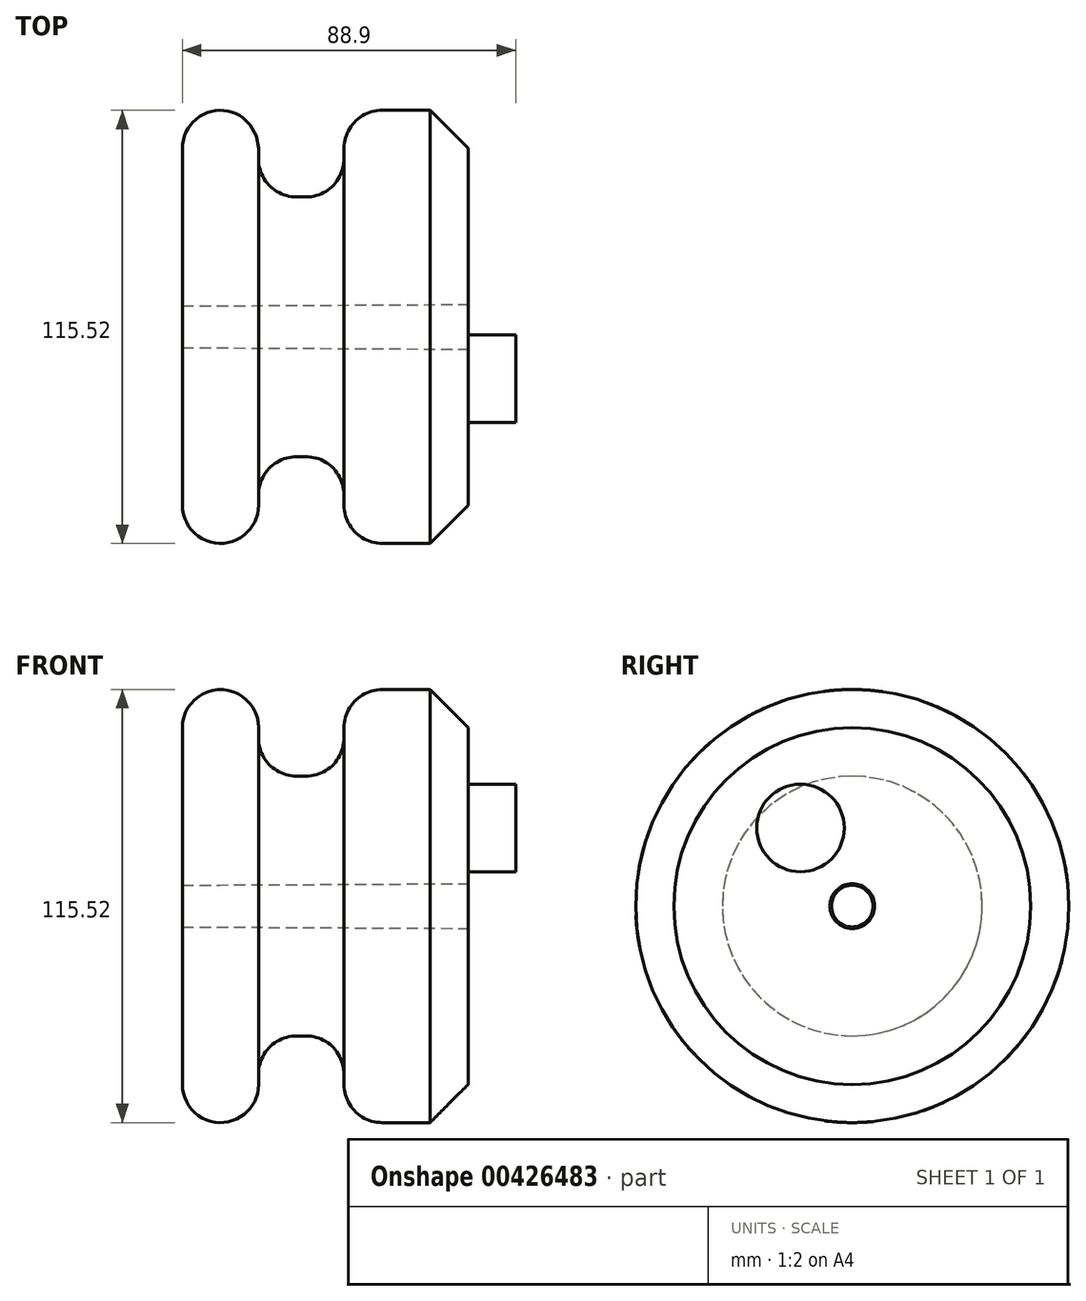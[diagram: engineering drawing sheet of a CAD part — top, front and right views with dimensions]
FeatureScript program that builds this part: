
annotation { "Feature Type Name" : "Feature", "Feature Type Description" : "" }
export const myFeature = defineFeature(function(context is Context, id is Id, definition is map)
    precondition{}
    {
        {
            var Q0;
            Q0=qCreatedBy(makeId("Top.planeOp"),FACE);
            var sketch = newSketch(context, id + "F0", { "sketchPlane" : qUnion([Q0])});
            skLineSegment(sketch, "E0", {"start": v(-62.92, -5.56) * mm, "end": v(-62.92, -57.76) * mm});
            skLineSegment(sketch, "E1", {"start": v(-42.6, -57.76) * mm, "end": v(-42.6, -34.64) * mm});
            skLineSegment(sketch, "E2", {"start": v(-42.6, -34.64) * mm, "end": v(-19.82, -34.64) * mm});
            skLineSegment(sketch, "E3", {"start": v(-19.82, -34.64) * mm, "end": v(-19.82, -57.76) * mm});
            skLineSegment(sketch, "E4", {"start": v(-19.82, -57.76) * mm, "end": v(13.28, -57.76) * mm});
            skLineSegment(sketch, "E5", {"start": v(13.28, -57.76) * mm, "end": v(13.28, -5.97) * mm});
            skLineSegment(sketch, "E6", {"start": v(13.28, -5.97) * mm, "end": v(-62.92, -5.56) * mm});
            skLineSegment(sketch, "E7", {"start": v(-42.6, -57.76) * mm, "end": v(-62.92, -57.76) * mm});
            skLineSegment(sketch, "E8", {"start": v(-61.6, 0) * mm, "end": v(66.9, 0) * mm, "construction": true});
            skSolve(sketch);
        }
        {
            var Q0;
            Q0=makeQuery(id+"F0.imprint","IMPRINT",FACE,{"disambiguationData":[TD([[makeQuery(id+"F0.imprint","IMPRINT",EDGE,{"derivedFrom":sQuery(id+"F0.wireOp",EDGE,"E0")}),1.0]])]});
            var Q1;
            Q1=sQuery(id+"F0.wireOp",EDGE,"E8");
            revolve(context, id + "F1", {"entities" : qUnion([Q0]), "axis" : qUnion([Q1]), "revolveType" : RevolveType.FULL});
        }
        {
            var Q0;
            Q0=makeQuery(id+"F1.opRevolve","SWEPT_EDGE",EDGE,{"disambiguationData":[OSD([sQuery(id+"F0.wireOp",EDGE,"E0"),sQuery(id+"F0.wireOp",EDGE,"E7")])]});
            fillet(context, id + "F2", {"entities" : qUnion([Q0]), "radius" : 10.16 * mm, "tangentPropagation" : true, "allowEdgeOverflow" : false});
        }
        {
            var Q0;
            Q0=makeQuery(id+"F1.opRevolve","SWEPT_EDGE",EDGE,{"disambiguationData":[OSD([sQuery(id+"F0.wireOp",EDGE,"E3"),sQuery(id+"F0.wireOp",EDGE,"E4")])]});
            var Q1;
            {var subQ0=sQuery(id+"F0.wireOp",EDGE,"E4");Q1=makeQuery(id+"F39CXcwR2j7VM4l_1.opFillet","BLEND_EDGE",EDGE,{"blendedFrom":[makeQuery(id+"F1.opRevolve","SWEPT_EDGE",EDGE,{"disambiguationData":[OSD([subQ0,sQuery(id+"F0.wireOp",EDGE,"E5")])]}),makeQuery(id+"F1.opRevolve","SWEPT_FACE",FACE,{"disambiguationData":[OSD([subQ0])]})],"blendedInto":[makeQuery(id+"F1.opRevolve","SWEPT_FACE",FACE,{"disambiguationData":[OSD([subQ0])]})]});}
            var Q2;
            Q2=makeQuery(id+"F1.opRevolve","SWEPT_EDGE",EDGE,{"disambiguationData":[OSD([sQuery(id+"F0.wireOp",EDGE,"E2"),sQuery(id+"F0.wireOp",EDGE,"E3")])]});
            var Q3;
            Q3=makeQuery(id+"F1.opRevolve","SWEPT_EDGE",EDGE,{"disambiguationData":[OSD([sQuery(id+"F0.wireOp",EDGE,"E1"),sQuery(id+"F0.wireOp",EDGE,"E7")])]});
            var Q4;
            {var subQ0=sQuery(id+"F0.wireOp",EDGE,"E7");Q4=makeQuery(id+"F2.opFillet","BLEND_EDGE",EDGE,{"blendedFrom":[makeQuery(id+"F1.opRevolve","SWEPT_EDGE",EDGE,{"disambiguationData":[OSD([sQuery(id+"F0.wireOp",EDGE,"E0"),subQ0])]}),makeQuery(id+"F1.opRevolve","SWEPT_FACE",FACE,{"disambiguationData":[OSD([subQ0])]})],"blendedInto":[makeQuery(id+"F1.opRevolve","SWEPT_FACE",FACE,{"disambiguationData":[OSD([subQ0])]})]});}
            var Q5;
            {var subQ0=sQuery(id+"F0.wireOp",EDGE,"E5");Q5=makeQuery(id+"F39CXcwR2j7VM4l_1.opFillet","BLEND_EDGE",EDGE,{"blendedFrom":[makeQuery(id+"F1.opRevolve","SWEPT_EDGE",EDGE,{"disambiguationData":[OSD([sQuery(id+"F0.wireOp",EDGE,"E4"),subQ0])]}),makeQuery(id+"F1.opRevolve","SWEPT_FACE",FACE,{"disambiguationData":[OSD([subQ0])]})],"blendedInto":[makeQuery(id+"F1.opRevolve","SWEPT_FACE",FACE,{"disambiguationData":[OSD([subQ0])]})]});}
            var Q6;
            Q6=makeQuery(id+"F1.opRevolve","SWEPT_EDGE",EDGE,{"disambiguationData":[OSD([sQuery(id+"F0.wireOp",EDGE,"E1"),sQuery(id+"F0.wireOp",EDGE,"E2")])]});
            fillet(context, id + "F3", {"entities" : qUnion([Q0, Q1, Q2, Q3, Q4, Q5, Q6]), "radius" : 10.16 * mm, "tangentPropagation" : true, "allowEdgeOverflow" : false});
        }
        {
            var Q0;
            Q0=makeQuery(id+"F1.opRevolve","SWEPT_EDGE",EDGE,{"disambiguationData":[OSD([sQuery(id+"F0.wireOp",EDGE,"E4"),sQuery(id+"F0.wireOp",EDGE,"E5")])]});
            chamfer(context, id + "F4", {"entities" : qUnion([Q0]), "width" : 10.16 * mm, "tangentPropagation" : true});
        }
        {
            var Q0;
            Q0=makeQuery(id+"F1.opRevolve","SWEPT_FACE",FACE,{"disambiguationData":[OSD([sQuery(id+"F0.wireOp",EDGE,"E5")])]});
            var sketch = newSketch(context, id + "F5", { "sketchPlane" : qUnion([Q0])});
            skCircle(sketch, "E9", {"center": v(-13.81, 20.83) * mm, "radius": 11.67 * mm});
            skSolve(sketch);
        }
        {
            var Q0;
            Q0=makeQuery(id+"F5.imprint","IMPRINT",FACE,{"disambiguationData":[TD([[makeQuery(id+"F5.imprint","IMPRINT",EDGE,{"derivedFrom":sQuery(id+"F5.wireOp",EDGE,"E9")}),1.0]])]});
            extrude(context, id + "F6", {"entities" : qUnion([Q0]), "operationType" : NewBodyOperationType.ADD, "depth" : 12.7 * mm});
        }
    });
